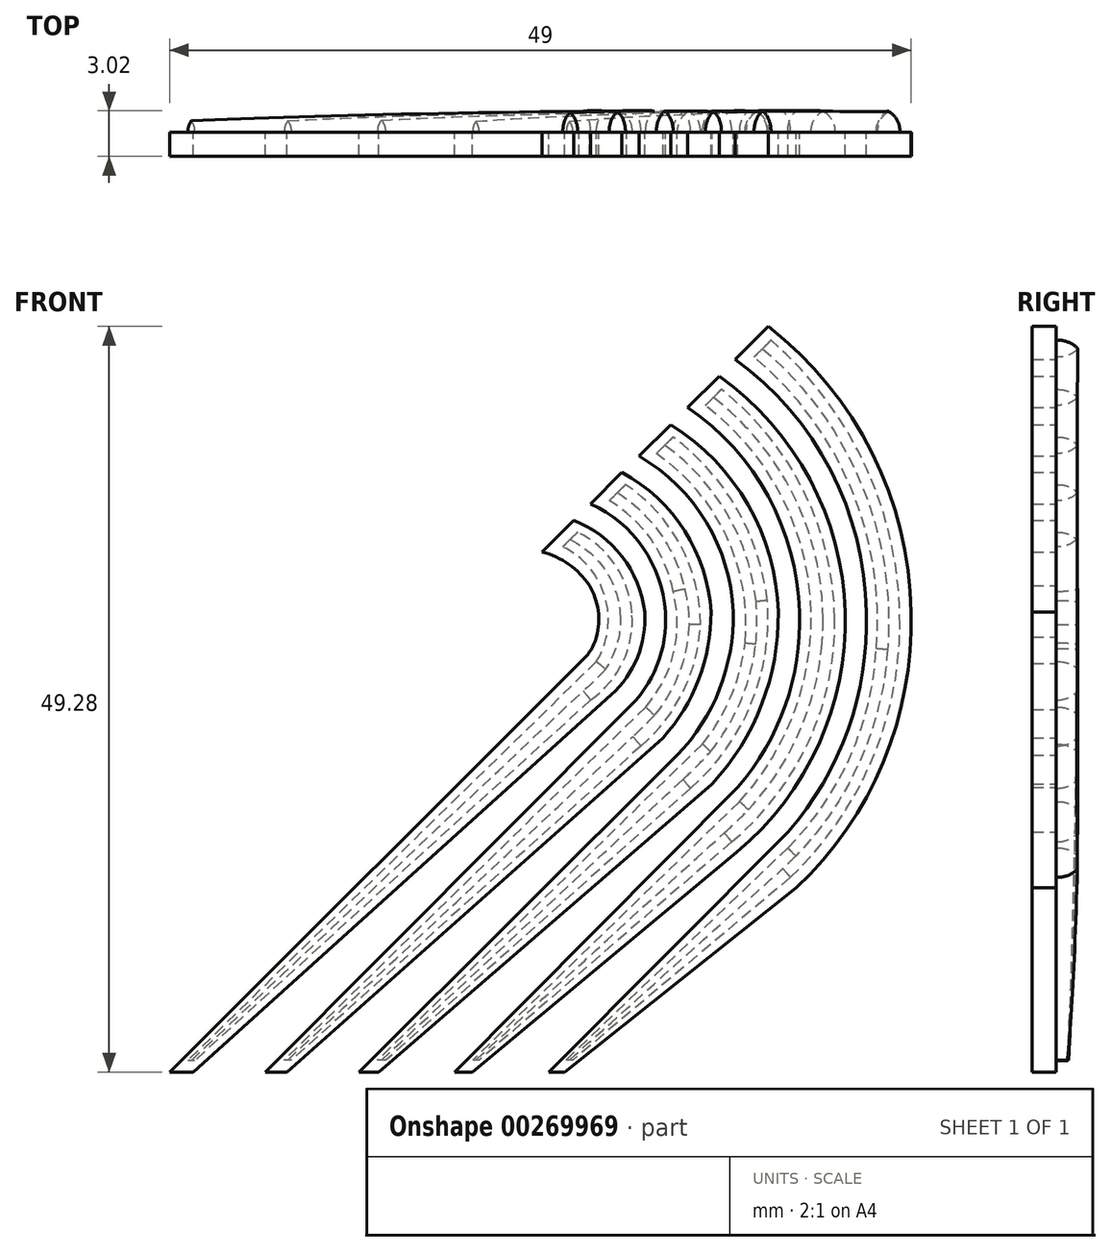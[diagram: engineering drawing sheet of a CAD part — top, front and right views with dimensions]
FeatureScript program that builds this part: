
annotation { "Feature Type Name" : "Feature", "Feature Type Description" : "" }
export const myFeature = defineFeature(function(context is Context, id is Id, definition is map)
    precondition{}
    {
        {
            var Q0;
            Q0=qCreatedBy(makeId("Front.planeOp"),FACE);
            var sketch = newSketch(context, id + "F0", { "sketchPlane" : qUnion([Q0])});
            skLineSegment(sketch, "E0", {"start": v(-5.94, 10.25) * mm, "end": v(-3.84, 12.33) * mm});
            skLineSegment(sketch, "E1", {"start": v(-2.73, 13.43) * mm, "end": v(-0.66, 15.5) * mm});
            skArc(sketch, "E2", {"start": v(-2.81, 8.03) * mm, "mid": v(-4.17, 9.43) * mm, "end": v(-5.94, 10.25) * mm});
            skArc(sketch, "E3", {"start": v(-2.35, 4.63) * mm, "mid": v(-2.24, 6.38) * mm, "end": v(-2.81, 8.03) * mm});
            skArc(sketch, "E4", {"start": v(-3.5, 2.89) * mm, "mid": v(-2.8, 3.67) * mm, "end": v(-2.35, 4.63) * mm});
            skLineSegment(sketch, "E5", {"start": v(-3.5, 2.89) * mm, "end": v(-30.55, -24.13) * mm});
            skLineSegment(sketch, "E6", {"start": v(-30.55, -24.13) * mm, "end": v(-29, -24.13) * mm});
            skLineSegment(sketch, "E7", {"start": v(-29, -24.13) * mm, "end": v(-1.37, 0.8) * mm});
            skArc(sketch, "E8", {"start": v(-1.37, 0.8) * mm, "mid": v(0.36, 3.28) * mm, "end": v(0.84, 6.27) * mm});
            skArc(sketch, "E9", {"start": v(0.84, 6.27) * mm, "mid": v(-0.66, 9.95) * mm, "end": v(-3.84, 12.33) * mm});
            skArc(sketch, "E10", {"start": v(2.21, 6.27) * mm, "mid": v(0.73, 10.53) * mm, "end": v(-2.73, 13.43) * mm});
            skArc(sketch, "E11", {"start": v(-0.35, -0.18) * mm, "mid": v(1.65, 2.76) * mm, "end": v(2.21, 6.27) * mm});
            skLineSegment(sketch, "E12", {"start": v(-0.35, -0.18) * mm, "end": v(-24.24, -24.13) * mm});
            skLineSegment(sketch, "E13", {"start": v(-24.24, -24.13) * mm, "end": v(-22.82, -24.13) * mm});
            skLineSegment(sketch, "E14", {"start": v(-22.82, -24.13) * mm, "end": v(2.05, -2.05) * mm});
            skArc(sketch, "E15", {"start": v(2.05, -2.05) * mm, "mid": v(4.41, 1.81) * mm, "end": v(5.22, 6.27) * mm});
            skArc(sketch, "E16", {"start": v(5.22, 6.27) * mm, "mid": v(3.48, 11.65) * mm, "end": v(-0.66, 15.5) * mm});
            skArc(sketch, "E17", {"start": v(6.68, 6.27) * mm, "mid": v(4.9, 12.23) * mm, "end": v(0.47, 16.58) * mm});
            skArc(sketch, "E18", {"start": v(2.99, -3.18) * mm, "mid": v(5.79, 1.17) * mm, "end": v(6.68, 6.27) * mm});
            skLineSegment(sketch, "E19", {"start": v(2.99, -3.18) * mm, "end": v(-18.03, -24.13) * mm});
            skLineSegment(sketch, "E20", {"start": v(-18.03, -24.13) * mm, "end": v(-16.73, -24.13) * mm});
            skLineSegment(sketch, "E21", {"start": v(-16.73, -24.13) * mm, "end": v(5.29, -5.09) * mm});
            skArc(sketch, "E22", {"start": v(5.29, -5.09) * mm, "mid": v(8.57, 0.17) * mm, "end": v(9.66, 6.27) * mm});
            skArc(sketch, "E23", {"start": v(9.66, 6.27) * mm, "mid": v(7.68, 13.35) * mm, "end": v(2.58, 18.65) * mm});
            skLineSegment(sketch, "E24", {"start": v(0.47, 16.58) * mm, "end": v(2.58, 18.65) * mm});
            skLineSegment(sketch, "E25", {"start": v(-11.72, -24.13) * mm, "end": v(-10.55, -24.13) * mm});
            skLineSegment(sketch, "E26", {"start": v(-10.55, -24.13) * mm, "end": v(6.93, -9.59) * mm});
            skLineSegment(sketch, "E27", {"start": v(-11.72, -24.13) * mm, "end": v(6.97, -5.32) * mm});
            skArc(sketch, "E28", {"start": v(6.97, -5.32) * mm, "mid": v(10.12, 0.08) * mm, "end": v(11.07, 6.27) * mm});
            skArc(sketch, "E29", {"start": v(6.93, -9.59) * mm, "mid": v(12.33, -2.48) * mm, "end": v(14.09, 6.27) * mm});
            skArc(sketch, "E30", {"start": v(11.07, 6.27) * mm, "mid": v(9, 13.92) * mm, "end": v(3.68, 19.79) * mm});
            skArc(sketch, "E31", {"start": v(14.09, 6.27) * mm, "mid": v(11.76, 15.04) * mm, "end": v(5.76, 21.86) * mm});
            skLineSegment(sketch, "E32", {"start": v(3.68, 19.79) * mm, "end": v(5.76, 21.86) * mm});
            skLineSegment(sketch, "E33", {"start": v(6.83, 22.97) * mm, "end": v(9, 25.15) * mm});
            skArc(sketch, "E34", {"start": v(15.47, 6.27) * mm, "mid": v(13.12, 15.64) * mm, "end": v(6.83, 22.97) * mm});
            skArc(sketch, "E35", {"start": v(18.45, 6.27) * mm, "mid": v(15.87, 16.79) * mm, "end": v(9, 25.15) * mm});
            skArc(sketch, "E36", {"start": v(10.3, -8.26) * mm, "mid": v(14.28, -1.5) * mm, "end": v(15.47, 6.27) * mm});
            skArc(sketch, "E37", {"start": v(10.86, -11.97) * mm, "mid": v(16.6, -3.66) * mm, "end": v(18.45, 6.27) * mm});
            skLineSegment(sketch, "E38", {"start": v(10.3, -8.26) * mm, "end": v(-5.5, -24.13) * mm});
            skLineSegment(sketch, "E39", {"start": v(-5.5, -24.13) * mm, "end": v(-4.46, -24.13) * mm});
            skLineSegment(sketch, "E40", {"start": v(-4.46, -24.13) * mm, "end": v(10.86, -11.97) * mm});
            skSolve(sketch);
        }
        {
            var Q0;
            Q0=makeQuery(id+"F0.imprint","IMPRINT",FACE,{"disambiguationData":[TD([[makeQuery(id+"F0.imprint","IMPRINT",EDGE,{"derivedFrom":sQuery(id+"F0.wireOp",EDGE,"E0")}),-1.0]])]});
            var Q1;
            Q1=makeQuery(id+"F0.imprint","IMPRINT",FACE,{"disambiguationData":[TD([[makeQuery(id+"F0.imprint","IMPRINT",EDGE,{"derivedFrom":sQuery(id+"F0.wireOp",EDGE,"E1")}),-1.0]])]});
            var Q2;
            Q2=makeQuery(id+"F0.imprint","IMPRINT",FACE,{"disambiguationData":[TD([[makeQuery(id+"F0.imprint","IMPRINT",EDGE,{"derivedFrom":sQuery(id+"F0.wireOp",EDGE,"E17")}),-1.0]])]});
            var Q3;
            Q3=makeQuery(id+"F0.imprint","IMPRINT",FACE,{"disambiguationData":[TD([[makeQuery(id+"F0.imprint","IMPRINT",EDGE,{"derivedFrom":sQuery(id+"F0.wireOp",EDGE,"E25")}),1.0]])]});
            var Q4;
            Q4=makeQuery(id+"F0.imprint","IMPRINT",FACE,{"disambiguationData":[TD([[makeQuery(id+"F0.imprint","IMPRINT",EDGE,{"derivedFrom":sQuery(id+"F0.wireOp",EDGE,"E33")}),-1.0]])]});
            extrude(context, id + "F1", {"entities" : qUnion([Q0, Q1, Q2, Q3, Q4]), "depth" : 1.59 * mm});
        }
        {
            var Q0;
            Q0=makeQuery(id+"F1.opExtrude","CAP_FACE",FACE,{"disambiguationData":[OSD([sQuery(id+"F0.wireOp",EDGE,"E33"),sQuery(id+"F0.wireOp",EDGE,"E34"),sQuery(id+"F0.wireOp",EDGE,"E35"),sQuery(id+"F0.wireOp",EDGE,"E36"),sQuery(id+"F0.wireOp",EDGE,"E37"),sQuery(id+"F0.wireOp",EDGE,"E38"),sQuery(id+"F0.wireOp",EDGE,"E39"),sQuery(id+"F0.wireOp",EDGE,"E40")])],"isStart":true});
            var sketch = newSketch(context, id + "F2", { "sketchPlane" : qUnion([Q0])});
            skLineSegment(sketch, "E41", {"start": v(-9, 24.06) * mm, "end": v(-9.19, 24.25) * mm});
            skPoint(sketch, "E41.startSnap0", {"position": v(-7.92, 24.06) * mm});
            skLineSegment(sketch, "E42", {"start": v(-9, 24.06) * mm, "end": v(-8.07, 23.12) * mm});
            skArc(sketch, "E43", {"start": v(-9.19, 24.25) * mm, "mid": v(-15.52, 15.74) * mm, "end": v(-17.7, 5.36) * mm});
            skArc(sketch, "E44", {"start": v(-8.07, 23.12) * mm, "mid": v(-14.47, 14.5) * mm, "end": v(-16.14, 3.87) * mm});
            skArc(sketch, "E45", {"start": v(-17.7, 5.36) * mm, "mid": v(-15.78, -3.68) * mm, "end": v(-10.48, -11.26) * mm});
            skArc(sketch, "E46", {"start": v(-16.14, 3.87) * mm, "mid": v(-14.43, -3.26) * mm, "end": v(-10.3, -9.31) * mm});
            skLineSegment(sketch, "E47", {"start": v(-10.48, -11.26) * mm, "end": v(3.9, -23.34) * mm});
            skLineSegment(sketch, "E48", {"start": v(3.9, -23.34) * mm, "end": v(4.34, -23.34) * mm});
            skLineSegment(sketch, "E49", {"start": v(4.34, -23.34) * mm, "end": v(-10.3, -9.31) * mm});
            skPoint(sketch, "E50.orphan", {"position": v(-7.13, 22.19) * mm});
            skSolve(sketch);
        }
        {
            var Q0;
            Q0=makeQuery(id+"F2.imprint","IMPRINT",FACE,{"disambiguationData":[TD([[makeQuery(id+"F2.imprint","IMPRINT",EDGE,{"derivedFrom":sQuery(id+"F2.wireOp",EDGE,"E41")}),1.0]])]});
            extrude(context, id + "F3", {"entities" : qUnion([Q0]), "operationType" : NewBodyOperationType.ADD, "depth" : 1.6 * mm});
        }
        {
            var Q0;
            Q0=makeQuery(id+"F3.opExtrude","CAP_EDGE",EDGE,{"disambiguationData":[OSD([sQuery(id+"F2.wireOp",EDGE,"E43")])],"isStart":false});
            var Q1;
            Q1=makeQuery(id+"F3.opExtrude","CAP_EDGE",EDGE,{"disambiguationData":[OSD([sQuery(id+"F2.wireOp",EDGE,"E44")])],"isStart":false});
            var Q2;
            Q2=makeQuery(id+"F3.opExtrude","CAP_EDGE",EDGE,{"disambiguationData":[OSD([sQuery(id+"F2.wireOp",EDGE,"E45")])],"isStart":false});
            var Q3;
            Q3=makeQuery(id+"F3.opExtrude","CAP_EDGE",EDGE,{"disambiguationData":[OSD([sQuery(id+"F2.wireOp",EDGE,"E46")])],"isStart":false});
            var Q4;
            Q4=makeQuery(id+"F3.opExtrude","CAP_EDGE",EDGE,{"disambiguationData":[OSD([sQuery(id+"F2.wireOp",EDGE,"E47")])],"isStart":false});
            var Q5;
            Q5=makeQuery(id+"F3.opExtrude","CAP_EDGE",EDGE,{"disambiguationData":[OSD([sQuery(id+"F2.wireOp",EDGE,"E49")])],"isStart":false});
            fillet(context, id + "F4", {"entities" : qUnion([Q0, Q1, Q2, Q3, Q4, Q5]), "radius" : 1.52 * mm, "tangentPropagation" : true, "allowEdgeOverflow" : false});
        }
        {
            var Q0;
            Q0=makeQuery(id+"F1.opExtrude","CAP_FACE",FACE,{"disambiguationData":[OSD([sQuery(id+"F0.wireOp",EDGE,"E25"),sQuery(id+"F0.wireOp",EDGE,"E26"),sQuery(id+"F0.wireOp",EDGE,"E27"),sQuery(id+"F0.wireOp",EDGE,"E28"),sQuery(id+"F0.wireOp",EDGE,"E29"),sQuery(id+"F0.wireOp",EDGE,"E30"),sQuery(id+"F0.wireOp",EDGE,"E31"),sQuery(id+"F0.wireOp",EDGE,"E32")])],"isStart":true});
            var sketch = newSketch(context, id + "F5", { "sketchPlane" : qUnion([Q0])});
            skLineSegment(sketch, "E51", {"start": v(-5.91, 21) * mm, "end": v(-4.85, 19.93) * mm});
            skArc(sketch, "E52", {"start": v(-5.91, 21) * mm, "mid": v(-11.37, 14.25) * mm, "end": v(-13.4, 5.82) * mm});
            skArc(sketch, "E53", {"start": v(-4.85, 19.93) * mm, "mid": v(-10.4, 12.86) * mm, "end": v(-11.74, 3.99) * mm});
            skArc(sketch, "E54", {"start": v(-11.74, 3.99) * mm, "mid": v(-10.24, -1.5) * mm, "end": v(-7.12, -6.25) * mm});
            skArc(sketch, "E55", {"start": v(-13.4, 5.82) * mm, "mid": v(-11.66, -2.31) * mm, "end": v(-6.6, -8.91) * mm});
            skLineSegment(sketch, "E56", {"start": v(10.1, -23.34) * mm, "end": v(10.53, -23.34) * mm});
            skLineSegment(sketch, "E57", {"start": v(-6.6, -8.91) * mm, "end": v(10.1, -23.34) * mm});
            skLineSegment(sketch, "E58", {"start": v(-7.12, -6.25) * mm, "end": v(10.53, -23.34) * mm});
            skPoint(sketch, "E59.orphan", {"position": v(-8.08, 23.15) * mm});
            skPoint(sketch, "E60.orphan", {"position": v(-3.74, 18.83) * mm});
            skSolve(sketch);
        }
        {
            var Q0;
            Q0=makeQuery(id+"F5.imprint","IMPRINT",FACE,{"disambiguationData":[TD([[makeQuery(id+"F5.imprint","IMPRINT",EDGE,{"derivedFrom":sQuery(id+"F5.wireOp",EDGE,"E51")}),-1.0]])]});
            extrude(context, id + "F6", {"entities" : qUnion([Q0]), "operationType" : NewBodyOperationType.ADD, "depth" : 1.6 * mm});
        }
        {
            var Q0;
            Q0=makeQuery(id+"F6.opExtrude","CAP_EDGE",EDGE,{"disambiguationData":[OSD([sQuery(id+"F5.wireOp",EDGE,"E57")])],"isStart":false});
            var Q1;
            Q1=makeQuery(id+"F6.opExtrude","CAP_EDGE",EDGE,{"disambiguationData":[OSD([sQuery(id+"F5.wireOp",EDGE,"E58")])],"isStart":false});
            var Q2;
            Q2=makeQuery(id+"F6.opExtrude","CAP_EDGE",EDGE,{"disambiguationData":[OSD([sQuery(id+"F5.wireOp",EDGE,"E55")])],"isStart":false});
            var Q3;
            Q3=makeQuery(id+"F6.opExtrude","CAP_EDGE",EDGE,{"disambiguationData":[OSD([sQuery(id+"F5.wireOp",EDGE,"E54")])],"isStart":false});
            var Q4;
            Q4=makeQuery(id+"F6.opExtrude","CAP_EDGE",EDGE,{"disambiguationData":[OSD([sQuery(id+"F5.wireOp",EDGE,"E53")])],"isStart":false});
            var Q5;
            Q5=makeQuery(id+"F6.opExtrude","CAP_EDGE",EDGE,{"disambiguationData":[OSD([sQuery(id+"F5.wireOp",EDGE,"E52")])],"isStart":false});
            fillet(context, id + "F7", {"entities" : qUnion([Q0, Q1, Q2, Q3, Q4, Q5]), "radius" : 1.52 * mm, "tangentPropagation" : true, "allowEdgeOverflow" : false});
        }
        {
            var Q0;
            Q0=makeQuery(id+"F1.opExtrude","CAP_FACE",FACE,{"disambiguationData":[OSD([sQuery(id+"F0.wireOp",EDGE,"E17"),sQuery(id+"F0.wireOp",EDGE,"E18"),sQuery(id+"F0.wireOp",EDGE,"E19"),sQuery(id+"F0.wireOp",EDGE,"E20"),sQuery(id+"F0.wireOp",EDGE,"E21"),sQuery(id+"F0.wireOp",EDGE,"E22"),sQuery(id+"F0.wireOp",EDGE,"E23"),sQuery(id+"F0.wireOp",EDGE,"E24")])],"isStart":true});
            var sketch = newSketch(context, id + "F8", { "sketchPlane" : qUnion([Q0])});
            skLineSegment(sketch, "E61", {"start": v(-2.72, 17.84) * mm, "end": v(-1.6, 16.76) * mm});
            skArc(sketch, "E62", {"start": v(-2.72, 17.84) * mm, "mid": v(-6.94, 13.08) * mm, "end": v(-8.94, 7.04) * mm});
            skArc(sketch, "E63", {"start": v(-1.6, 16.76) * mm, "mid": v(-6.24, 11.3) * mm, "end": v(-7.47, 4.24) * mm});
            skArc(sketch, "E64", {"start": v(-8.94, 7.04) * mm, "mid": v(-7.88, 0.23) * mm, "end": v(-3.87, -5.37) * mm});
            skArc(sketch, "E65", {"start": v(-7.47, 4.24) * mm, "mid": v(-6.54, 0.7) * mm, "end": v(-4.67, -2.45) * mm});
            skLineSegment(sketch, "E66", {"start": v(16.27, -23.35) * mm, "end": v(16.82, -23.35) * mm});
            skLineSegment(sketch, "E67", {"start": v(-3.87, -5.37) * mm, "end": v(16.27, -23.35) * mm});
            skLineSegment(sketch, "E68", {"start": v(-4.67, -2.45) * mm, "end": v(16.82, -23.35) * mm});
            skPoint(sketch, "E69.orphan", {"position": v(-0.55, 15.72) * mm});
            skPoint(sketch, "E70.orphan", {"position": v(-4.9, 19.97) * mm});
            skSolve(sketch);
        }
        {
            var Q0;
            Q0=makeQuery(id+"F8.imprint","IMPRINT",FACE,{"disambiguationData":[TD([[makeQuery(id+"F8.imprint","IMPRINT",EDGE,{"derivedFrom":sQuery(id+"F8.wireOp",EDGE,"E61")}),-1.0]])]});
            extrude(context, id + "F9", {"entities" : qUnion([Q0]), "operationType" : NewBodyOperationType.ADD, "depth" : 1.6 * mm});
        }
        {
            var Q0;
            Q0=makeQuery(id+"F9.opExtrude","CAP_EDGE",EDGE,{"disambiguationData":[OSD([sQuery(id+"F8.wireOp",EDGE,"E67")])],"isStart":false});
            var Q1;
            Q1=makeQuery(id+"F9.opExtrude","CAP_EDGE",EDGE,{"disambiguationData":[OSD([sQuery(id+"F8.wireOp",EDGE,"E64")])],"isStart":false});
            var Q2;
            Q2=makeQuery(id+"F9.opExtrude","CAP_EDGE",EDGE,{"disambiguationData":[OSD([sQuery(id+"F8.wireOp",EDGE,"E68")])],"isStart":false});
            var Q3;
            Q3=makeQuery(id+"F9.opExtrude","CAP_EDGE",EDGE,{"disambiguationData":[OSD([sQuery(id+"F8.wireOp",EDGE,"E65")])],"isStart":false});
            var Q4;
            Q4=makeQuery(id+"F9.opExtrude","CAP_EDGE",EDGE,{"disambiguationData":[OSD([sQuery(id+"F8.wireOp",EDGE,"E63")])],"isStart":false});
            var Q5;
            Q5=makeQuery(id+"F9.opExtrude","CAP_EDGE",EDGE,{"disambiguationData":[OSD([sQuery(id+"F8.wireOp",EDGE,"E62")])],"isStart":false});
            fillet(context, id + "F10", {"entities" : qUnion([Q0, Q1, Q2, Q3, Q4, Q5]), "radius" : 1.52 * mm, "tangentPropagation" : true, "allowEdgeOverflow" : false});
        }
        {
            var Q0;
            Q0=makeQuery(id+"F1.opExtrude","CAP_FACE",FACE,{"disambiguationData":[OSD([sQuery(id+"F0.wireOp",EDGE,"E1"),sQuery(id+"F0.wireOp",EDGE,"E10"),sQuery(id+"F0.wireOp",EDGE,"E11"),sQuery(id+"F0.wireOp",EDGE,"E12"),sQuery(id+"F0.wireOp",EDGE,"E13"),sQuery(id+"F0.wireOp",EDGE,"E14"),sQuery(id+"F0.wireOp",EDGE,"E15"),sQuery(id+"F0.wireOp",EDGE,"E16")])],"isStart":true});
            var sketch = newSketch(context, id + "F11", { "sketchPlane" : qUnion([Q0])});
            skLineSegment(sketch, "E71", {"start": v(0.43, 14.7) * mm, "end": v(1.5, 13.63) * mm});
            skArc(sketch, "E72", {"start": v(0.43, 14.7) * mm, "mid": v(-3.2, 10.7) * mm, "end": v(-4.53, 5.44) * mm});
            skArc(sketch, "E73", {"start": v(-4.53, 5.44) * mm, "mid": v(-3.38, 1.03) * mm, "end": v(-0.6, -2.57) * mm});
            skArc(sketch, "E74", {"start": v(1.5, 13.63) * mm, "mid": v(-1.25, 11.1) * mm, "end": v(-2.72, 7.65) * mm});
            skLineSegment(sketch, "E75", {"start": v(22.5, -23.34) * mm, "end": v(22.98, -23.34) * mm});
            skLineSegment(sketch, "E76", {"start": v(-0.6, -2.57) * mm, "end": v(22.5, -23.34) * mm});
            skArc(sketch, "E77", {"start": v(-2.72, 7.65) * mm, "mid": v(-2.76, 3.6) * mm, "end": v(-0.9, 0) * mm});
            skLineSegment(sketch, "E78", {"start": v(-0.9, 0) * mm, "end": v(22.98, -23.34) * mm});
            skSolve(sketch);
        }
        {
            var Q0;
            Q0=makeQuery(id+"F11.imprint","IMPRINT",FACE,{"disambiguationData":[TD([[makeQuery(id+"F11.imprint","IMPRINT",EDGE,{"derivedFrom":sQuery(id+"F11.wireOp",EDGE,"E71")}),-1.0]])]});
            extrude(context, id + "F12", {"entities" : qUnion([Q0]), "operationType" : NewBodyOperationType.ADD, "depth" : 1.6 * mm});
        }
        {
            var Q0;
            Q0=makeQuery(id+"F12.opExtrude","CAP_EDGE",EDGE,{"disambiguationData":[OSD([sQuery(id+"F11.wireOp",EDGE,"E72")])],"isStart":false});
            var Q1;
            Q1=makeQuery(id+"F12.opExtrude","CAP_EDGE",EDGE,{"disambiguationData":[OSD([sQuery(id+"F11.wireOp",EDGE,"E73")])],"isStart":false});
            var Q2;
            Q2=makeQuery(id+"F12.opExtrude","CAP_EDGE",EDGE,{"disambiguationData":[OSD([sQuery(id+"F11.wireOp",EDGE,"E76")])],"isStart":false});
            var Q3;
            Q3=makeQuery(id+"F12.opExtrude","CAP_EDGE",EDGE,{"disambiguationData":[OSD([sQuery(id+"F11.wireOp",EDGE,"E78")])],"isStart":false});
            var Q4;
            Q4=makeQuery(id+"F12.opExtrude","CAP_EDGE",EDGE,{"disambiguationData":[OSD([sQuery(id+"F11.wireOp",EDGE,"E77")])],"isStart":false});
            var Q5;
            Q5=makeQuery(id+"F12.opExtrude","CAP_EDGE",EDGE,{"disambiguationData":[OSD([sQuery(id+"F11.wireOp",EDGE,"E74")])],"isStart":false});
            fillet(context, id + "F13", {"entities" : qUnion([Q0, Q1, Q2, Q3, Q4, Q5]), "radius" : 1.52 * mm, "tangentPropagation" : true, "allowEdgeOverflow" : false});
        }
        {
            var Q0;
            Q0=makeQuery(id+"F1.opExtrude","CAP_FACE",FACE,{"disambiguationData":[OSD([sQuery(id+"F0.wireOp",EDGE,"E0"),sQuery(id+"F0.wireOp",EDGE,"E2"),sQuery(id+"F0.wireOp",EDGE,"E3"),sQuery(id+"F0.wireOp",EDGE,"E4"),sQuery(id+"F0.wireOp",EDGE,"E5"),sQuery(id+"F0.wireOp",EDGE,"E6"),sQuery(id+"F0.wireOp",EDGE,"E7"),sQuery(id+"F0.wireOp",EDGE,"E8"),sQuery(id+"F0.wireOp",EDGE,"E9")])],"isStart":true});
            var sketch = newSketch(context, id + "F14", { "sketchPlane" : qUnion([Q0])});
            skLineSegment(sketch, "E79", {"start": v(3.6, 11.56) * mm, "end": v(4.57, 10.58) * mm});
            skLineSegment(sketch, "E80", {"start": v(28.89, -23.36) * mm, "end": v(29.35, -23.36) * mm});
            skLineSegment(sketch, "E81", {"start": v(2.35, 3) * mm, "end": v(29.35, -23.36) * mm});
            skPoint(sketch, "E82.orphan", {"position": v(1.5, 13.63) * mm});
            skPoint(sketch, "E83.orphan", {"position": v(5.68, 9.48) * mm});
            skArc(sketch, "E84", {"start": v(4.57, 10.58) * mm, "mid": v(1.78, 7.28) * mm, "end": v(2.35, 3) * mm});
            skArc(sketch, "E85", {"start": v(3.6, 11.56) * mm, "mid": v(1.1, 9.36) * mm, "end": v(0, 6.22) * mm});
            skArc(sketch, "E86", {"start": v(0, 6.22) * mm, "mid": v(0.6, 2.98) * mm, "end": v(2.73, 0.47) * mm});
            skLineSegment(sketch, "E87", {"start": v(2.73, 0.47) * mm, "end": v(28.89, -23.36) * mm});
            skSolve(sketch);
        }
        {
            var Q0;
            Q0=makeQuery(id+"F14.imprint","IMPRINT",FACE,{"disambiguationData":[TD([[makeQuery(id+"F14.imprint","IMPRINT",EDGE,{"derivedFrom":sQuery(id+"F14.wireOp",EDGE,"E79")}),-1.0]])]});
            extrude(context, id + "F15", {"entities" : qUnion([Q0]), "operationType" : NewBodyOperationType.ADD, "depth" : 1.6 * mm});
        }
        {
            var Q0;
            Q0=makeQuery(id+"F15.opExtrude","CAP_EDGE",EDGE,{"disambiguationData":[OSD([sQuery(id+"F14.wireOp",EDGE,"E85")])],"isStart":false});
            var Q1;
            Q1=makeQuery(id+"F15.opExtrude","CAP_EDGE",EDGE,{"disambiguationData":[OSD([sQuery(id+"F14.wireOp",EDGE,"E86")])],"isStart":false});
            var Q2;
            Q2=makeQuery(id+"F15.opExtrude","CAP_EDGE",EDGE,{"disambiguationData":[OSD([sQuery(id+"F14.wireOp",EDGE,"E87")])],"isStart":false});
            var Q3;
            Q3=makeQuery(id+"F15.opExtrude","CAP_EDGE",EDGE,{"disambiguationData":[OSD([sQuery(id+"F14.wireOp",EDGE,"E81")])],"isStart":false});
            var Q4;
            Q4=makeQuery(id+"F15.opExtrude","CAP_EDGE",EDGE,{"disambiguationData":[OSD([sQuery(id+"F14.wireOp",EDGE,"E84")])],"isStart":false});
            fillet(context, id + "F16", {"entities" : qUnion([Q0, Q1, Q2, Q3, Q4]), "radius" : 1.52 * mm, "tangentPropagation" : true, "allowEdgeOverflow" : false});
        }
    });
